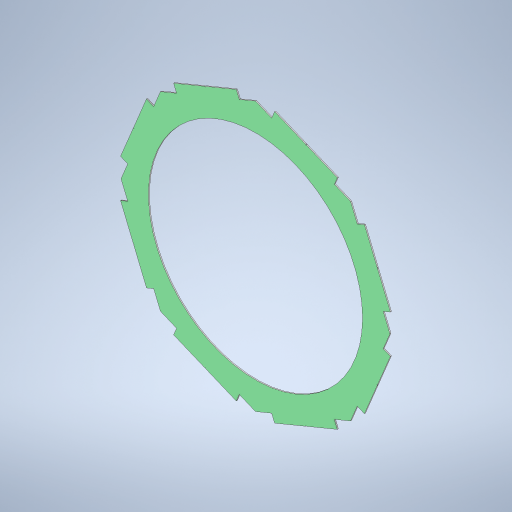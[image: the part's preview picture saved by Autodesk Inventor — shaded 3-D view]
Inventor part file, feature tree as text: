
AUTODESK INVENTOR PART (.ipt)
format: ipt  version: 2024.2 (Build 282272000, 272)  size: 397,312 bytes
history: native  units: mm
features: sketch x3, extrude x2, pattern_circular x2, other x2, sheet_metal_op x1
ambient origin geometry x8: Origin, YZ Plane, XZ Plane, XY Plane, X Axis, Y Axis, Z Axis, Center Point
bodies: Solid1 (feature_tree)
feature tree (10):
  sheet_metal_op  "Face1"
  sketch  "Sketch5"  dims[d26=413.0mm]
  extrude  "Extrusion2"  Depth=509.0mm
  pattern_circular  "Circular Pattern2"  [2 undecoded]
  extrude  "Extrusion3"  Depth=15.0mm TaperAngle=360.0deg
  pattern_circular  "Circular Pattern3"  Count=4  [1 undecoded]
  sketch  "Sketch2"  dims[d15=2.0mm d23=509.0mm]
  other  "Plate1"
  sketch  "Sketch6"  dims[d30=1.0mm d31=10.0mm d32=0.0mm d33=80.0mm d34=360.0deg d36=40.0mm d37=15.0mm d38=0.0mm d39=0.0mm d40=80.0mm d41=360.0deg]
  other  "Definition1"
note: 3 required parameter values undecoded (feature->parameter linkage not recoverable at this tier; creation-order binding heuristic only, values carry confidence <= 0.55)
